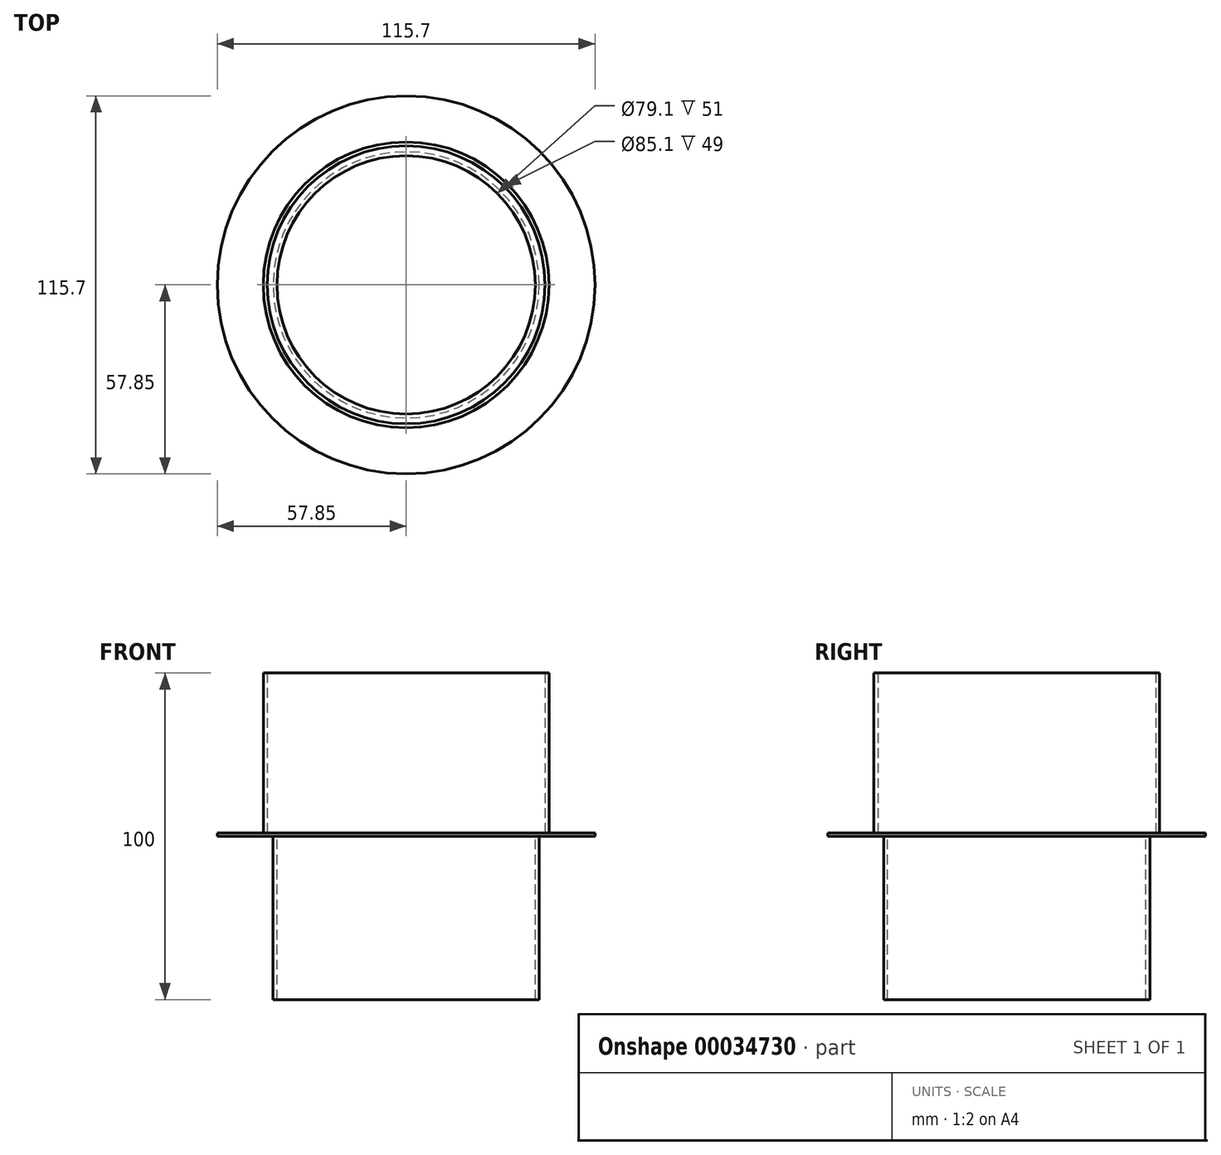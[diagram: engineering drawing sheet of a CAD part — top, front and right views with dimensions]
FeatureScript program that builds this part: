
annotation { "Feature Type Name" : "Feature", "Feature Type Description" : "" }
export const myFeature = defineFeature(function(context is Context, id is Id, definition is map)
    precondition{}
    {
        {
            var Q0;
            Q0=qCreatedBy(makeId("Top.planeOp"),FACE);
            var sketch = newSketch(context, id + "F0", { "sketchPlane" : qUnion([Q0])});
            skCircle(sketch, "E0", {"center": v(0, 0) * mm, "radius": 40.75 * mm});
            skCircle(sketch, "E1.0", {"center": v(0, 0) * mm, "radius": 39.55 * mm});
            skCircle(sketch, "E2.0", {"center": v(0, 0) * mm, "radius": 57.85 * mm});
            skCircle(sketch, "E3.0", {"center": v(0, 0) * mm, "radius": 42.55 * mm});
            skCircle(sketch, "E4.0", {"center": v(0, 0) * mm, "radius": 43.75 * mm});
            skSolve(sketch);
        }
        {
            var Q0;
            Q0=makeQuery(id+"F0.imprint","IMPRINT",FACE,{"disambiguationData":[TD([[makeQuery(id+"F0.imprint","IMPRINT",EDGE,{"derivedFrom":sQuery(id+"F0.wireOp",EDGE,"E0")}),1.0]])]});
            extrude(context, id + "F1", {"entities" : qUnion([Q0]), "oppositeDirection" : true, "depth" : 50 * mm, "offsetDistance" : 25 * mm});
        }
        {
            var Q0;
            Q0=makeQuery(id+"F0.imprint","IMPRINT",FACE,{"disambiguationData":[TD([[makeQuery(id+"F0.imprint","IMPRINT",EDGE,{"derivedFrom":sQuery(id+"F0.wireOp",EDGE,"E2.0")}),1.0]])]});
            var Q1;
            Q1=makeQuery(id+"F0.imprint","IMPRINT",FACE,{"disambiguationData":[TD([[makeQuery(id+"F0.imprint","IMPRINT",EDGE,{"derivedFrom":sQuery(id+"F0.wireOp",EDGE,"E0")}),-1.0]])]});
            var Q2;
            Q2=makeQuery(id+"F0.imprint","IMPRINT",FACE,{"disambiguationData":[TD([[makeQuery(id+"F0.imprint","IMPRINT",EDGE,{"derivedFrom":sQuery(id+"F0.wireOp",EDGE,"E3.0")}),-1.0]])]});
            var Q3;
            Q3=makeQuery(id+"F0.imprint","IMPRINT",FACE,{"disambiguationData":[TD([[makeQuery(id+"F0.imprint","IMPRINT",EDGE,{"derivedFrom":sQuery(id+"F0.wireOp",EDGE,"E0")}),1.0]])]});
            extrude(context, id + "F2", {"entities" : qUnion([Q0, Q1, Q2, Q3]), "operationType" : NewBodyOperationType.ADD, "depth" : 1 * mm, "offsetDistance" : 25 * mm});
        }
        {
            var Q0;
            Q0=makeQuery(id+"F0.imprint","IMPRINT",FACE,{"disambiguationData":[TD([[makeQuery(id+"F0.imprint","IMPRINT",EDGE,{"derivedFrom":sQuery(id+"F0.wireOp",EDGE,"E3.0")}),-1.0]])]});
            extrude(context, id + "F3", {"entities" : qUnion([Q0]), "operationType" : NewBodyOperationType.ADD, "depth" : 50 * mm, "offsetDistance" : 25 * mm});
        }
    });
